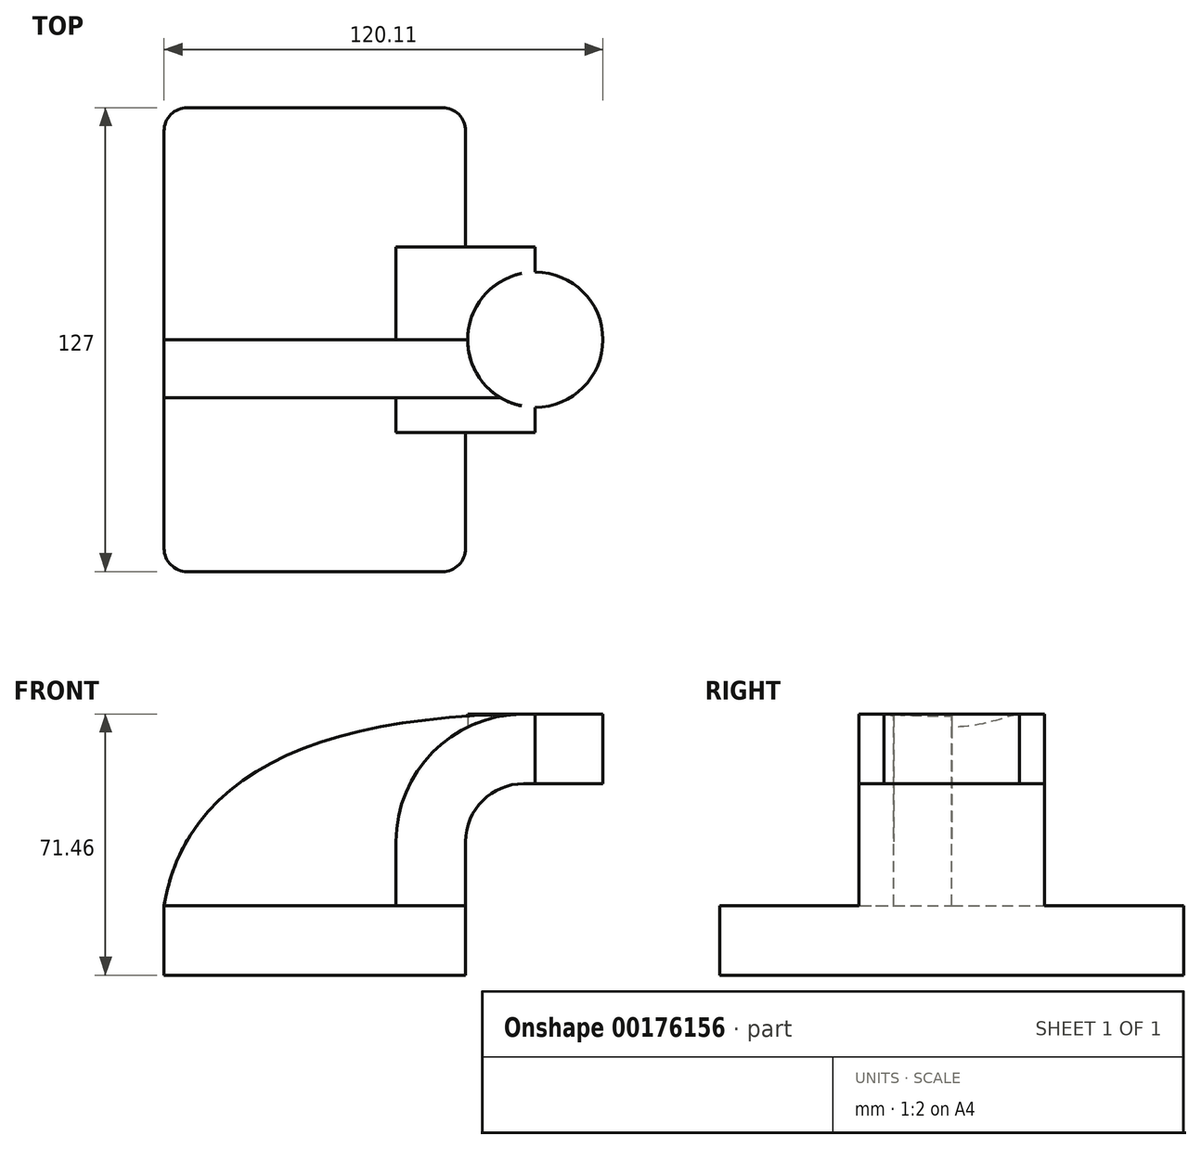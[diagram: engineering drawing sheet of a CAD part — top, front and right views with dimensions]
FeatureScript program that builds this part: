
annotation { "Feature Type Name" : "Feature", "Feature Type Description" : "" }
export const myFeature = defineFeature(function(context is Context, id is Id, definition is map)
    precondition{}
    {
        {
            var Q0;
            Q0=qCreatedBy(makeId("Front.planeOp"),FACE);
            var sketch = newSketch(context, id + "F0", { "sketchPlane" : qUnion([Q0])});
            skLineSegment(sketch, "E0.bottom", {"start": v(41.27, 9.53) * mm, "end": v(-41.28, 9.53) * mm});
            skLineSegment(sketch, "E0.top", {"start": v(41.28, -9.52) * mm, "end": v(-41.27, -9.52) * mm});
            skLineSegment(sketch, "E0.left", {"start": v(41.28, 9.53) * mm, "end": v(41.28, -9.52) * mm});
            skLineSegment(sketch, "E0.right", {"start": v(-41.28, 9.53) * mm, "end": v(-41.28, -9.52) * mm});
            skPoint(sketch, "E0.middle", {"position": v(0, 0) * mm});
            skLineSegment(sketch, "E1.bottom", {"start": v(111.12, 38.1) * mm, "end": v(60.32, 38.1) * mm});
            skLineSegment(sketch, "E1.top", {"start": v(111.12, 66.68) * mm, "end": v(60.32, 66.68) * mm});
            skLineSegment(sketch, "E1.left", {"start": v(111.12, 38.1) * mm, "end": v(111.12, 66.68) * mm});
            skLineSegment(sketch, "E1.right", {"start": v(60.32, 38.1) * mm, "end": v(60.32, 66.68) * mm});
            skPoint(sketch, "E1.middle", {"position": v(85.72, 52.39) * mm});
            skLineSegment(sketch, "E2", {"start": v(41.27, 9.53) * mm, "end": v(41.27, 27) * mm});
            skArc(sketch, "E3", {"start": v(41.27, 27) * mm, "mid": v(45.92, 38.23) * mm, "end": v(57.15, 42.88) * mm});
            skLineSegment(sketch, "E4", {"start": v(57.15, 42.88) * mm, "end": v(78.83, 42.88) * mm});
            skLineSegment(sketch, "E5.0", {"start": v(57.15, 61.93) * mm, "end": v(78.83, 61.93) * mm});
            skArc(sketch, "E5.1", {"start": v(22.22, 27) * mm, "mid": v(32.45, 51.7) * mm, "end": v(57.15, 61.93) * mm});
            skLineSegment(sketch, "E5.2", {"start": v(22.22, 9.53) * mm, "end": v(22.22, 27) * mm});
            skLineSegment(sketch, "E6", {"start": v(78.83, 61.93) * mm, "end": v(78.83, 42.88) * mm});
            skFitSpline(sketch, "E7", {"points": [v(-41.28, 9.52) * mm, v(57.15, 61.93) * mm], "startDerivative": vector(17, 102.02) * mm, "endDerivative": vector(179.27, 1.4) * mm});
            skSolve(sketch);
        }
        {
            var Q0;
            Q0=makeQuery(id+"F0.imprint","IMPRINT",FACE,{"disambiguationData":[TD([[makeQuery(id+"F0.imprint","IMPRINT",EDGE,{"derivedFrom":sQuery(id+"F0.wireOp",EDGE,"E0.top")}),-1.0]])]});
            extrude(context, id + "F1", {"entities" : qUnion([Q0]), "endBound" : BoundingType.SYMMETRIC, "depth" : 127 * mm});
        }
        {
            var Q0;
            {var subQ1=sQuery(id+"F0.wireOp",EDGE,"E2");Q0=makeQuery(id+"F0.imprint","IMPRINT",FACE,{"disambiguationData":[TD([[makeQuery(id+"F0.imprint","IMPRINT",EDGE,{"derivedFrom":subQ1}),1.0]])]});}
            extrude(context, id + "F2", {"entities" : qUnion([Q0]), "operationType" : NewBodyOperationType.ADD, "endBound" : BoundingType.SYMMETRIC, "depth" : 50.8 * mm});
        }
        {
            var Q0;
            {var subQ3=sQuery(id+"F0.wireOp",EDGE,"E5.2");Q0=makeQuery(id+"F0.imprint","IMPRINT",FACE,{"disambiguationData":[TD([[makeQuery(id+"F0.imprint","IMPRINT",EDGE,{"derivedFrom":subQ3}),1.0]])]});}
            extrude(context, id + "F3", {"entities" : qUnion([Q0]), "operationType" : NewBodyOperationType.ADD, "depth" : 15.88 * mm});
        }
        {
            var Q0;
            {var subQ5=sQuery(id+"F0.wireOp",EDGE,"E6");Q0=makeQuery(id+"F0.imprint","IMPRINT",FACE,{"disambiguationData":[TD([[makeQuery(id+"F0.imprint","IMPRINT",EDGE,{"derivedFrom":subQ5}),-1.0]])]});}
            var Q1;
            Q1=sQuery(id+"F0.wireOp",EDGE,"E1.right");
            revolve(context, id + "F4", {"operationType" : NewBodyOperationType.ADD, "entities" : qUnion([Q0]), "axis" : qUnion([Q1]), "revolveType" : RevolveType.FULL});
        }
        {
            var Q0;
            Q0=makeQuery(id+"F1.opExtrude","CAP_EDGE",EDGE,{"disambiguationData":[OSD([sQuery(id+"F0.wireOp",EDGE,"E0.left")])],"isStart":false});
            var Q1;
            Q1=makeQuery(id+"F1.opExtrude","CAP_EDGE",EDGE,{"disambiguationData":[OSD([sQuery(id+"F0.wireOp",EDGE,"E0.right")])],"isStart":false});
            var Q2;
            Q2=makeQuery(id+"F1.opExtrude","CAP_EDGE",EDGE,{"disambiguationData":[OSD([sQuery(id+"F0.wireOp",EDGE,"E0.left")])],"isStart":true});
            var Q3;
            Q3=makeQuery(id+"F1.opExtrude","CAP_EDGE",EDGE,{"disambiguationData":[OSD([sQuery(id+"F0.wireOp",EDGE,"E0.right")])],"isStart":true});
            fillet(context, id + "F5", {"entities" : qUnion([Q0, Q1, Q2, Q3]), "radius" : 6.35 * mm, "tangentPropagation" : true, "allowEdgeOverflow" : false});
        }
    });
